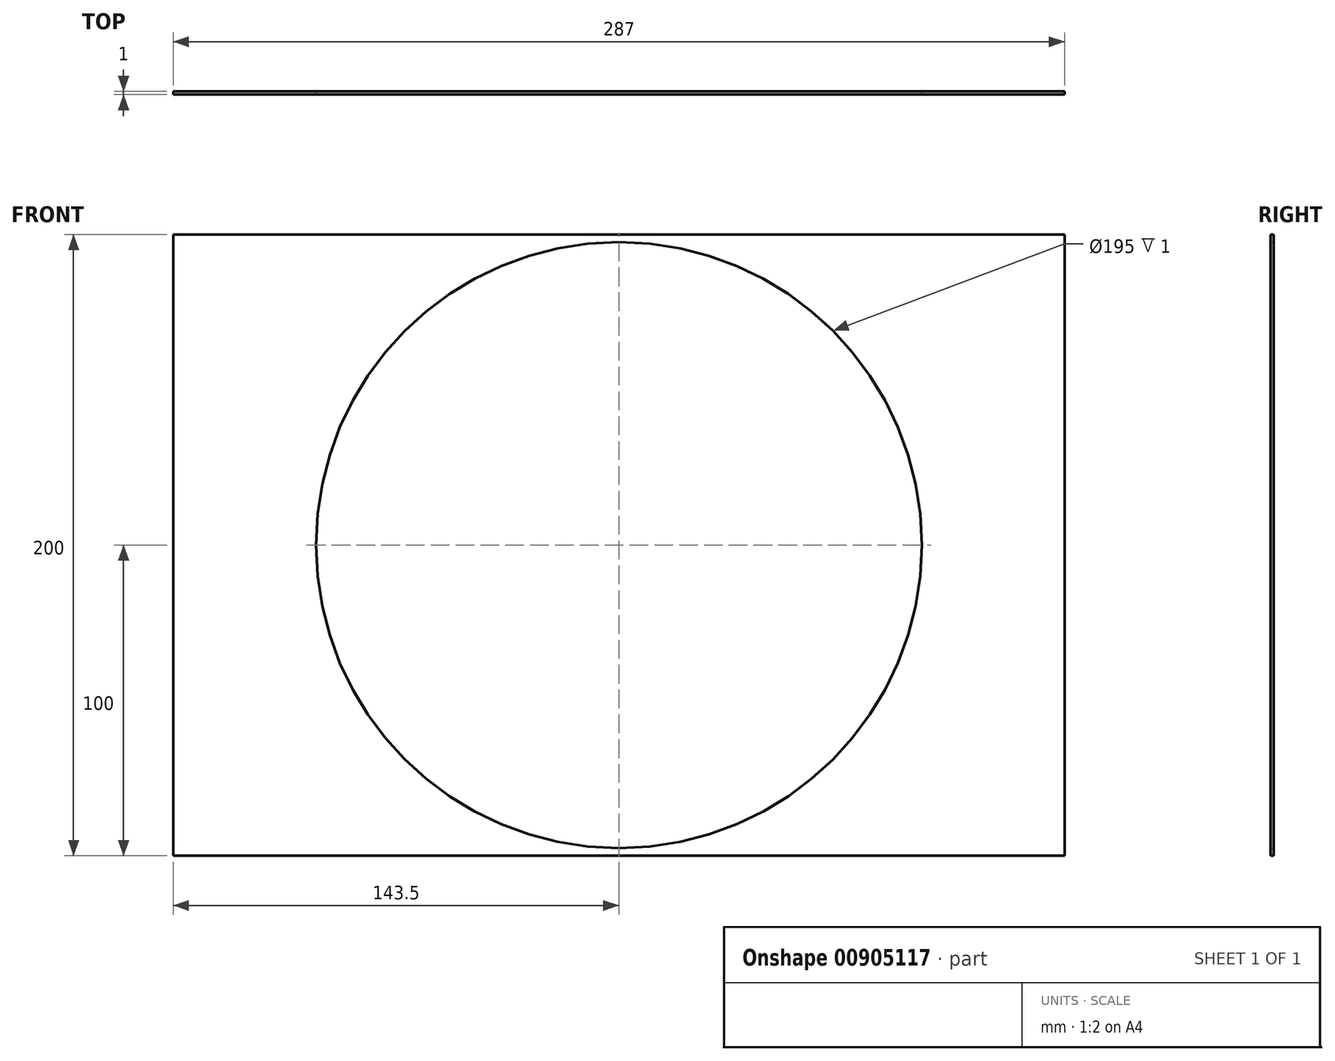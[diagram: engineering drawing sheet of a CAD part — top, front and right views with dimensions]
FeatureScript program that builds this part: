
annotation { "Feature Type Name" : "Feature", "Feature Type Description" : "" }
export const myFeature = defineFeature(function(context is Context, id is Id, definition is map)
    precondition{}
    {
        {
            var Q0;
            Q0=qCreatedBy(makeId("Front.planeOp"),FACE);
            var sketch = newSketch(context, id + "F0", { "sketchPlane" : qUnion([Q0])});
            skPoint(sketch, "E0.middle", {"position": v(0, 0) * mm});
            skCircle(sketch, "E1", {"center": v(0, 0) * mm, "radius": 97.5 * mm});
            skLineSegment(sketch, "E2.bottom", {"start": v(143.5, 100) * mm, "end": v(-143.5, 100) * mm});
            skLineSegment(sketch, "E2.top", {"start": v(143.5, -100) * mm, "end": v(-143.5, -100) * mm});
            skLineSegment(sketch, "E2.left", {"start": v(143.5, 100) * mm, "end": v(143.5, -100) * mm});
            skLineSegment(sketch, "E2.right", {"start": v(-143.5, 100) * mm, "end": v(-143.5, -100) * mm});
            skSolve(sketch);
        }
        {
            var Q0;
            Q0=makeQuery(id+"F0.imprint","IMPRINT",FACE,{"disambiguationData":[TD([[makeQuery(id+"F0.imprint","IMPRINT",EDGE,{"derivedFrom":sQuery(id+"F0.wireOp",EDGE,"E1")}),-1.0]])]});
            extrude(context, id + "F1", {"entities" : qUnion([Q0]), "depth" : 1 * mm, "offsetDistance" : 25 * mm});
        }
    });
